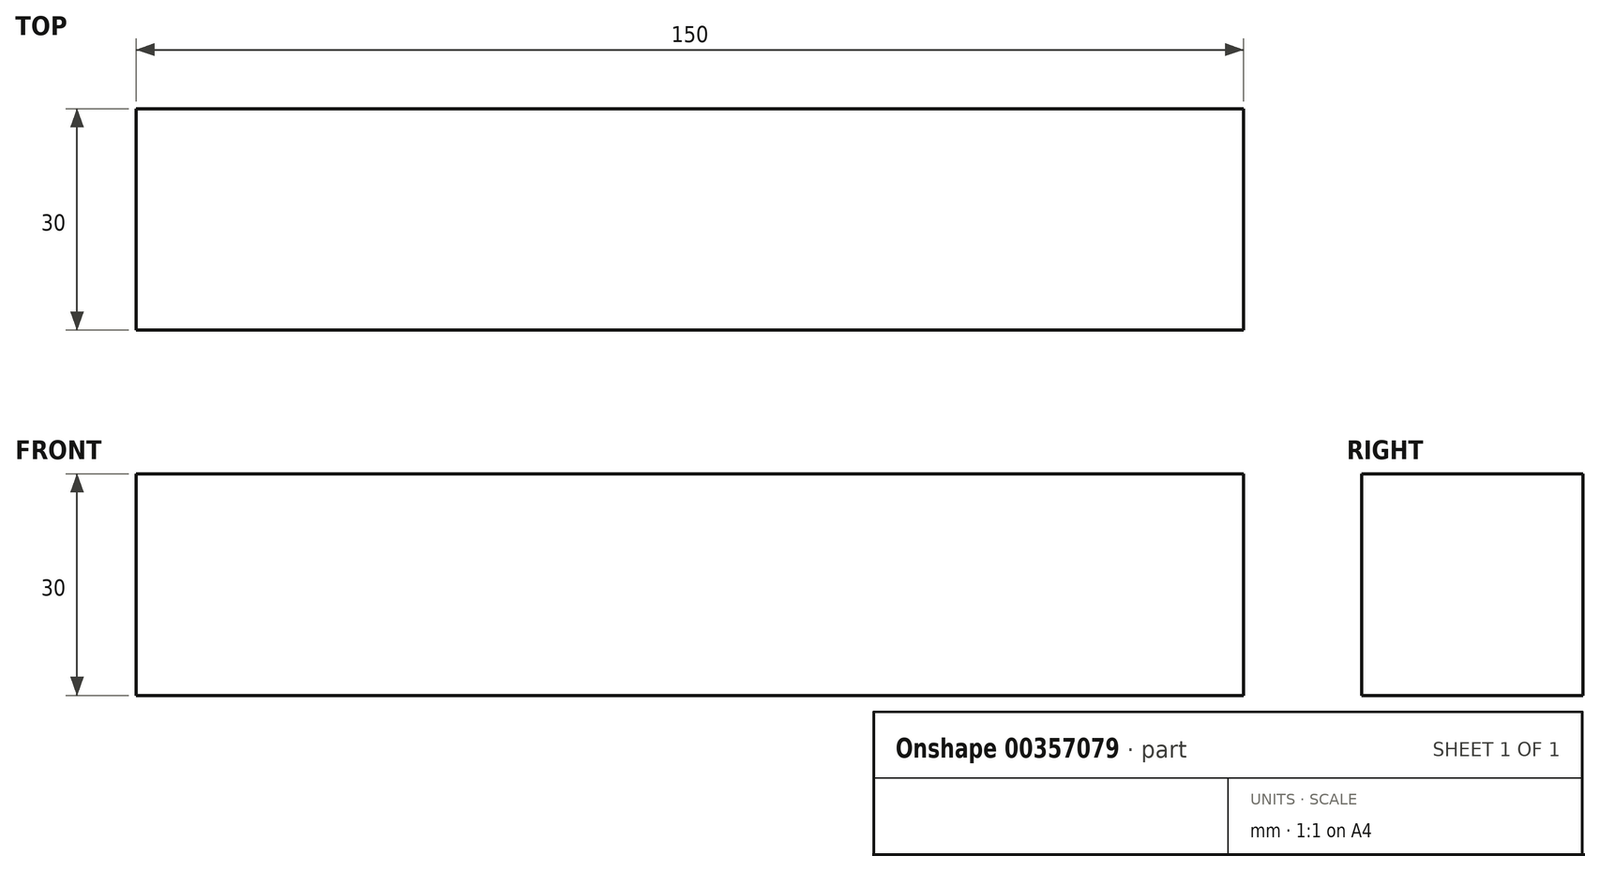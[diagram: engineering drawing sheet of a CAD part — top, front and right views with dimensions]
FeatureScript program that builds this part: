
annotation { "Feature Type Name" : "Feature", "Feature Type Description" : "" }
export const myFeature = defineFeature(function(context is Context, id is Id, definition is map)
    precondition{}
    {
        {
            var Q0;
            Q0=qCreatedBy(makeId("Front.planeOp"),FACE);
            var sketch = newSketch(context, id + "F0", { "sketchPlane" : qUnion([Q0])});
            skLineSegment(sketch, "E0.bottom", {"start": v(75, -15) * mm, "end": v(-75, -15) * mm});
            skLineSegment(sketch, "E0.top", {"start": v(75, 15) * mm, "end": v(-75, 15) * mm});
            skLineSegment(sketch, "E0.left", {"start": v(75, -15) * mm, "end": v(75, 15) * mm});
            skLineSegment(sketch, "E0.right", {"start": v(-75, -15) * mm, "end": v(-75, 15) * mm});
            skPoint(sketch, "E0.middle", {"position": v(0, 0) * mm});
            skSolve(sketch);
        }
        {
            var Q0;
            Q0=makeQuery(id+"F0.imprint","IMPRINT",FACE,{"disambiguationData":[TD([[makeQuery(id+"F0.imprint","IMPRINT",EDGE,{"derivedFrom":sQuery(id+"F0.wireOp",EDGE,"E0.bottom")}),-1.0]])]});
            extrude(context, id + "F1", {"entities" : qUnion([Q0]), "endBound" : BoundingType.SYMMETRIC, "depth" : 30 * mm});
        }
    });
